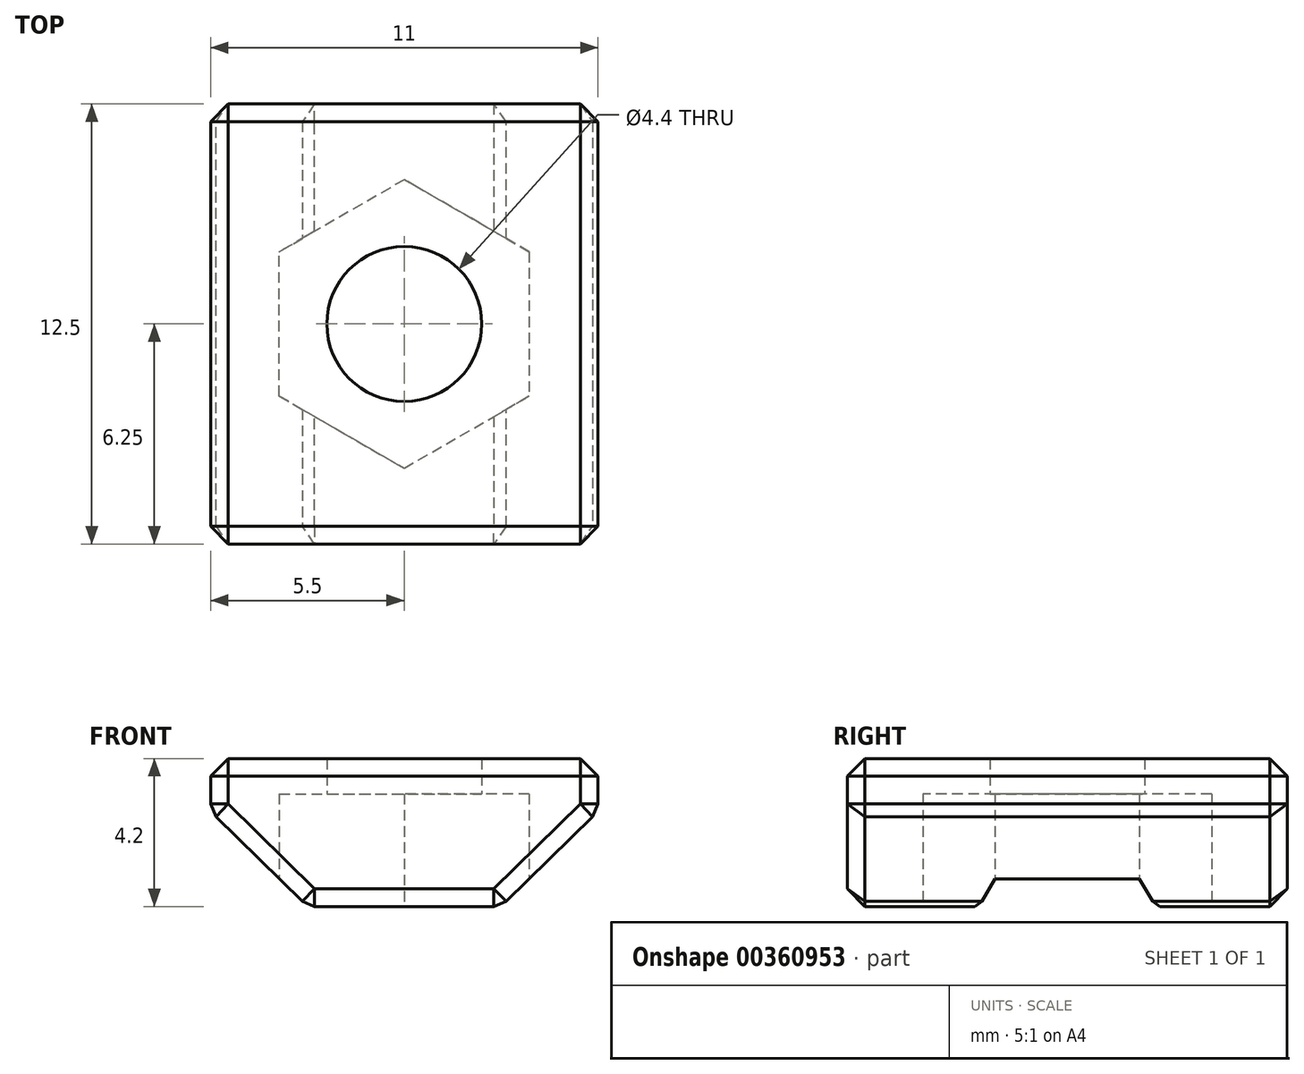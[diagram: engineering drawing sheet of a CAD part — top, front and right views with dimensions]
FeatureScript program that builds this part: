
annotation { "Feature Type Name" : "Feature", "Feature Type Description" : "" }
export const myFeature = defineFeature(function(context is Context, id is Id, definition is map)
    precondition{}
    {
        {
            var Q0;
            Q0=qCreatedBy(makeId("Front.planeOp"),FACE);
            var sketch = newSketch(context, id + "F0", { "sketchPlane" : qUnion([Q0])});
            skLineSegment(sketch, "E0", {"start": v(-2.75, 0) * mm, "end": v(2.75, 0) * mm});
            skLineSegment(sketch, "E1", {"start": v(2.75, 0) * mm, "end": v(5.5, 2.7) * mm});
            skLineSegment(sketch, "E2", {"start": v(-5.5, 2.7) * mm, "end": v(-2.75, 0) * mm});
            skLineSegment(sketch, "E3", {"start": v(5.5, 2.7) * mm, "end": v(5.5, 4.2) * mm});
            skLineSegment(sketch, "E4", {"start": v(5.5, 4.2) * mm, "end": v(-5.5, 4.2) * mm});
            skLineSegment(sketch, "E5", {"start": v(-5.5, 4.2) * mm, "end": v(-5.5, 2.7) * mm});
            skSolve(sketch);
        }
        {
            var Q0;
            Q0 = qSketchRegion(id + "F0", true);
            extrude(context, id + "F1", {"entities" : qUnion([Q0]), "depth" : 12.5 * mm});
        }
        {
            var Q0;
            Q0=makeQuery(id+"F1.opExtrude","SWEPT_FACE",FACE,{"disambiguationData":[OSD([sQuery(id+"F0.wireOp",EDGE,"E0")])]});
            var sketch = newSketch(context, id + "F2", { "sketchPlane" : qUnion([Q0])});
            skCircle(sketch, "E6.cCircle", {"center": v(0, 6.25) * mm, "radius": 3.55 * mm, "construction": true});
            skLineSegment(sketch, "E6.0", {"start": v(3.55, 8.3) * mm, "end": v(3.55, 4.2) * mm});
            skLineSegment(sketch, "E6.1", {"start": v(3.55, 4.2) * mm, "end": v(0, 2.15) * mm});
            skLineSegment(sketch, "E6.2", {"start": v(0, 2.15) * mm, "end": v(-3.55, 4.2) * mm});
            skLineSegment(sketch, "E6.3", {"start": v(-3.55, 4.2) * mm, "end": v(-3.55, 8.3) * mm});
            skLineSegment(sketch, "E6.4", {"start": v(-3.55, 8.3) * mm, "end": v(0, 10.35) * mm});
            skLineSegment(sketch, "E6.5", {"start": v(0, 10.35) * mm, "end": v(3.55, 8.3) * mm});
            skPoint(sketch, "E6.0.midPoint", {"position": v(3.55, 6.25) * mm});
            skSolve(sketch);
        }
        {
            var Q0;
            Q0 = qSketchRegion(id + "F2", true);
            extrude(context, id + "F3", {"entities" : qUnion([Q0]), "operationType" : NewBodyOperationType.REMOVE, "oppositeDirection" : true, "depth" : 3.2 * mm});
        }
        {
            var Q0;
            Q0=makeQuery(id+"F3.boolean.opBoolean","COPY",FACE,{"derivedFrom":makeQuery(id+"F3.opExtrude","CAP_FACE",FACE,{"disambiguationData":[OSD([sQuery(id+"F2.wireOp",EDGE,"E6.0"),sQuery(id+"F2.wireOp",EDGE,"E6.1"),sQuery(id+"F2.wireOp",EDGE,"E6.2"),sQuery(id+"F2.wireOp",EDGE,"E6.3"),sQuery(id+"F2.wireOp",EDGE,"E6.4"),sQuery(id+"F2.wireOp",EDGE,"E6.5")])],"isStart":false})});
            var sketch = newSketch(context, id + "F4", { "sketchPlane" : qUnion([Q0])});
            skCircle(sketch, "E7", {"center": v(0, 6.25) * mm, "radius": 2.2 * mm});
            skSolve(sketch);
        }
        {
            var Q0;
            Q0 = qSketchRegion(id + "F4", true);
            extrude(context, id + "F5", {"entities" : qUnion([Q0]), "operationType" : NewBodyOperationType.REMOVE, "oppositeDirection" : true, "depth" : 25 * mm});
        }
        {
            var Q0;
            Q0=makeQuery(id+"F1.opExtrude","SWEPT_EDGE",EDGE,{"disambiguationData":[OSD([sQuery(id+"F0.wireOp",EDGE,"E3"),sQuery(id+"F0.wireOp",EDGE,"E4")])]});
            var Q1;
            Q1=makeQuery(id+"F1.opExtrude","SWEPT_EDGE",EDGE,{"disambiguationData":[OSD([sQuery(id+"F0.wireOp",EDGE,"E1"),sQuery(id+"F0.wireOp",EDGE,"E3")])]});
            var Q2;
            Q2=makeQuery(id+"F1.opExtrude","SWEPT_EDGE",EDGE,{"disambiguationData":[OSD([sQuery(id+"F0.wireOp",EDGE,"E4"),sQuery(id+"F0.wireOp",EDGE,"E5")])]});
            var Q3;
            Q3=makeQuery(id+"F1.opExtrude","SWEPT_EDGE",EDGE,{"disambiguationData":[OSD([sQuery(id+"F0.wireOp",EDGE,"E2"),sQuery(id+"F0.wireOp",EDGE,"E5")])]});
            var Q4;
            Q4=makeQuery(id+"F1.opExtrude","CAP_EDGE",EDGE,{"disambiguationData":[OSD([sQuery(id+"F0.wireOp",EDGE,"E2")])],"isStart":true});
            var Q5;
            Q5=makeQuery(id+"F1.opExtrude","CAP_EDGE",EDGE,{"disambiguationData":[OSD([sQuery(id+"F0.wireOp",EDGE,"E5")])],"isStart":true});
            var Q6;
            Q6=makeQuery(id+"F1.opExtrude","CAP_EDGE",EDGE,{"disambiguationData":[OSD([sQuery(id+"F0.wireOp",EDGE,"E4")])],"isStart":true});
            var Q7;
            Q7=makeQuery(id+"F1.opExtrude","CAP_EDGE",EDGE,{"disambiguationData":[OSD([sQuery(id+"F0.wireOp",EDGE,"E3")])],"isStart":true});
            var Q8;
            Q8=makeQuery(id+"F1.opExtrude","CAP_EDGE",EDGE,{"disambiguationData":[OSD([sQuery(id+"F0.wireOp",EDGE,"E1")])],"isStart":true});
            var Q9;
            Q9=makeQuery(id+"F1.opExtrude","CAP_EDGE",EDGE,{"disambiguationData":[OSD([sQuery(id+"F0.wireOp",EDGE,"E0")])],"isStart":true});
            var Q10;
            Q10=makeQuery(id+"F1.opExtrude","CAP_FACE",FACE,{"disambiguationData":[OSD([sQuery(id+"F0.wireOp",EDGE,"E0"),sQuery(id+"F0.wireOp",EDGE,"E1"),sQuery(id+"F0.wireOp",EDGE,"E2"),sQuery(id+"F0.wireOp",EDGE,"E3"),sQuery(id+"F0.wireOp",EDGE,"E4"),sQuery(id+"F0.wireOp",EDGE,"E5")])],"isStart":false});
            var Q11;
            {var subQ0=sQuery(id+"F0.wireOp",EDGE,"E0");var subQ1=sQuery(id+"F0.wireOp",EDGE,"E1");Q11=makeQuery(id+"F3.boolean.opBoolean","SPLIT",EDGE,{"disambiguationData":[TD([makeQuery(id+"F3.opExtrude","SWEPT_FACE",FACE,{"disambiguationData":[OSD([sQuery(id+"F2.wireOp",EDGE,"E6.1")])]})])],"derivedFrom":makeQuery(id+"F1.opExtrude","SWEPT_EDGE",EDGE,{"disambiguationData":[OSD([subQ0,subQ1])]})});}
            var Q12;
            {var subQ0=sQuery(id+"F0.wireOp",EDGE,"E0");var subQ1=sQuery(id+"F0.wireOp",EDGE,"E2");Q12=makeQuery(id+"F3.boolean.opBoolean","SPLIT",EDGE,{"disambiguationData":[TD([makeQuery(id+"F3.opExtrude","SWEPT_FACE",FACE,{"disambiguationData":[OSD([sQuery(id+"F2.wireOp",EDGE,"E6.2")])]})])],"derivedFrom":makeQuery(id+"F1.opExtrude","SWEPT_EDGE",EDGE,{"disambiguationData":[OSD([subQ0,subQ1])]})});}
            var Q13;
            {var subQ0=sQuery(id+"F0.wireOp",EDGE,"E0");var subQ1=sQuery(id+"F0.wireOp",EDGE,"E2");Q13=makeQuery(id+"F3.boolean.opBoolean","SPLIT",EDGE,{"disambiguationData":[TD([makeQuery(id+"F3.opExtrude","SWEPT_FACE",FACE,{"disambiguationData":[OSD([sQuery(id+"F2.wireOp",EDGE,"E6.4")])]})])],"derivedFrom":makeQuery(id+"F1.opExtrude","SWEPT_EDGE",EDGE,{"disambiguationData":[OSD([subQ0,subQ1])]})});}
            var Q14;
            {var subQ0=sQuery(id+"F0.wireOp",EDGE,"E0");var subQ1=sQuery(id+"F0.wireOp",EDGE,"E1");Q14=makeQuery(id+"F3.boolean.opBoolean","SPLIT",EDGE,{"disambiguationData":[TD([makeQuery(id+"F3.opExtrude","SWEPT_FACE",FACE,{"disambiguationData":[OSD([sQuery(id+"F2.wireOp",EDGE,"E6.5")])]})])],"derivedFrom":makeQuery(id+"F1.opExtrude","SWEPT_EDGE",EDGE,{"disambiguationData":[OSD([subQ0,subQ1])]})});}
            chamfer(context, id + "F6", {"entities" : qUnion([Q0, Q1, Q2, Q3, Q4, Q5, Q6, Q7, Q8, Q9, Q10, Q11, Q12, Q13, Q14]), "width" : 0.5 * mm, "tangentPropagation" : true});
        }
    });
